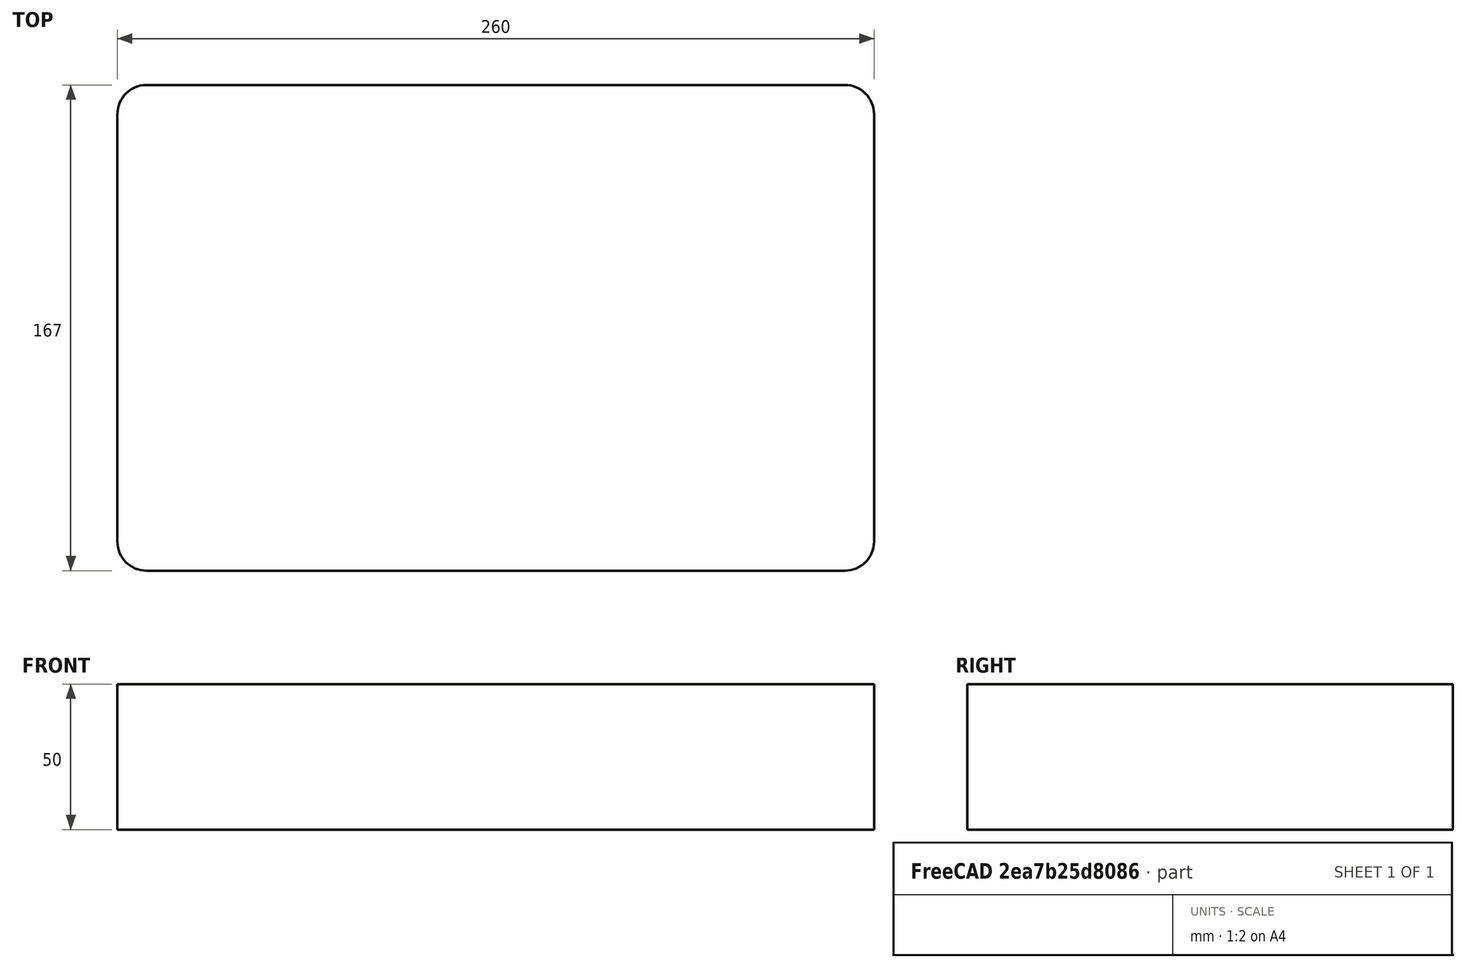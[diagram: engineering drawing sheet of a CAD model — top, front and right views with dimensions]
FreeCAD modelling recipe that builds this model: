
FCSTD DOCUMENT  (FreeCAD 0.20R29603 (Git))
Label: BoxCad1
License: All rights reserved
LicenseURL: http://en.wikipedia.org/wiki/All_rights_reserved
objects: PartDesign::Body×2, Sketcher::SketchObject×1, PartDesign::Pad×1
note: 5 computed .brp shape members not serialized (recipe doc carries the construction recipe); baked Part::Feature solids carry a one-line shape summary decoded from their .brp

FEATURE [PartDesign::Body] Body
  Origin = -> Origin
FEATURE [Sketcher::SketchObject] Sketch
  FullyConstrained = true
  MapMode = 5
  Support = -> [XY_Plane001]
  sketch-geometry (10):
    g0: ArcOfCircle CenterX=10 CenterY=157 CenterZ=0 NormalX=0 NormalY=0 NormalZ=1 AngleXU=0 Radius=10 StartAngle=1.5708 EndAngle=3.14159
    g1: LineSegment StartX=10 StartY=167 StartZ=0 EndX=250 EndY=167 EndZ=0
    g2: ArcOfCircle CenterX=250 CenterY=157 CenterZ=0 NormalX=0 NormalY=0 NormalZ=1 AngleXU=0 Radius=10 StartAngle=0 EndAngle=1.5708
    g3: LineSegment StartX=260 StartY=157 StartZ=0 EndX=260 EndY=10 EndZ=0
    g4: ArcOfCircle CenterX=250 CenterY=10 CenterZ=0 NormalX=0 NormalY=0 NormalZ=1 AngleXU=0 Radius=10 StartAngle=4.71239 EndAngle=6.28319
    g5: LineSegment StartX=250 StartY=0 StartZ=0 EndX=10 EndY=0 EndZ=0
    g6: ArcOfCircle CenterX=10 CenterY=10 CenterZ=0 NormalX=0 NormalY=0 NormalZ=1 AngleXU=0 Radius=10 StartAngle=3.14159 EndAngle=4.71239
    g7: LineSegment StartX=0 StartY=10 StartZ=0 EndX=0 EndY=157 EndZ=0
    g8: GeomPoint X=0 Y=167 Z=0
    g9: GeomPoint X=260 Y=0 Z=0
  constraints (24):
    c: Tangent(g0,g1) = 1.5708
    c: Tangent(g1,g2) = 1.5708
    c: Tangent(g2,g3) = 1.5708
    c: Tangent(g3,g4) = 1.5708
    c: Tangent(g4,g5) = 1.5708
    c: Tangent(g5,g6) = 1.5708
    c: Tangent(g6,g7) = 1.5708
    c: Tangent(g7,g0) = 1.5708
    c: Horizontal(g1)
    c: Horizontal(g5)
    c: Vertical(g3)
    c: Vertical(g7)
    c: Equal(g0,g2)
    c: Equal(g2,g4)
    c: Equal(g4,g6)
    c: PointOnObject(g8,g1)
    c: PointOnObject(g8,g7)
    c: PointOnObject(g9,g3)
    c: PointOnObject(g9,g5)
    c: PointOnObject(g8,g-2)
    c: PointOnObject(g9,g-1)
    c: Distance(g1) = 240
    c: DistanceY(g7,g7) = 147
    c: Radius(g0) = 10
FEATURE [PartDesign::Pad] Pad
  Direction = (0,0,1)
  Length = 50
  Length2 = 10
  Profile = -> Sketch
  ReferenceAxis = -> Sketch [N_Axis]
  Type = 0
FEATURE [PartDesign::Body] Body001
  Group = -> [Sketch,Pad]
  Origin = -> Origin001
  Tip = -> Pad
